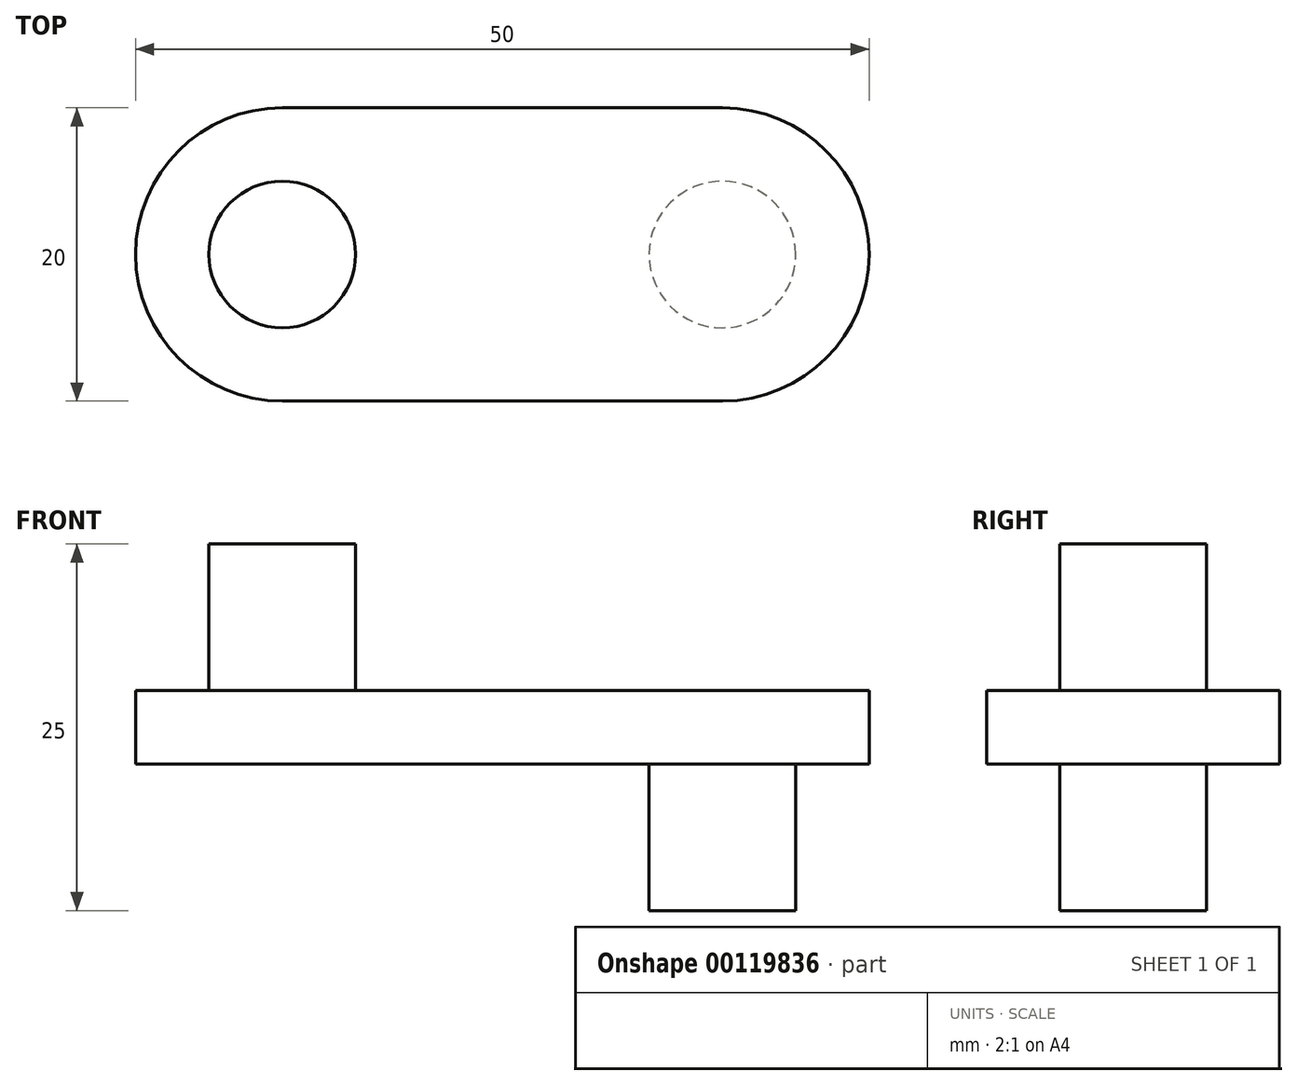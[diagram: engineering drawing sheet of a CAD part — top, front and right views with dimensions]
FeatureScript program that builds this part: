
annotation { "Feature Type Name" : "Feature", "Feature Type Description" : "" }
export const myFeature = defineFeature(function(context is Context, id is Id, definition is map)
    precondition{}
    {
        {
            var Q0;
            Q0=qCreatedBy(makeId("Top.planeOp"),FACE);
            var sketch = newSketch(context, id + "F0", { "sketchPlane" : qUnion([Q0])});
            skLineSegment(sketch, "E0.bottom", {"start": v(0, 0) * mm, "end": v(30, 0) * mm});
            skLineSegment(sketch, "E0.top", {"start": v(0, 20) * mm, "end": v(30, 20) * mm});
            skLineSegment(sketch, "E0.left", {"start": v(0, 0) * mm, "end": v(0, 20) * mm});
            skLineSegment(sketch, "E0.right", {"start": v(30, 0) * mm, "end": v(30, 20) * mm});
            skArc(sketch, "E1", {"start": v(0, 20) * mm, "mid": v(-10, 10) * mm, "end": v(0, 0) * mm});
            skArc(sketch, "E2", {"start": v(30, 0) * mm, "mid": v(40, 10) * mm, "end": v(30, 20) * mm});
            skCircle(sketch, "E3", {"center": v(0, 10) * mm, "radius": 5 * mm});
            skCircle(sketch, "E4", {"center": v(30, 10) * mm, "radius": 5 * mm});
            skSolve(sketch);
        }
        {
            var Q0;
            {var subQ5=sQuery(id+"F0.wireOp",EDGE,"E0.bottom");Q0=makeQuery(id+"F0.imprint","IMPRINT",FACE,{"disambiguationData":[TD([[makeQuery(id+"F0.imprint","IMPRINT",EDGE,{"derivedFrom":subQ5}),1.0]])]});}
            var Q1;
            {var subQ0=sQuery(id+"F0.wireOp",EDGE,"E1");Q1=makeQuery(id+"F0.imprint","IMPRINT",FACE,{"disambiguationData":[TD([[makeQuery(id+"F0.imprint","IMPRINT",EDGE,{"derivedFrom":subQ0}),1.0]])]});}
            var Q2;
            {var subQ0=sQuery(id+"F0.wireOp",EDGE,"E2");Q2=makeQuery(id+"F0.imprint","IMPRINT",FACE,{"disambiguationData":[TD([[makeQuery(id+"F0.imprint","IMPRINT",EDGE,{"derivedFrom":subQ0}),1.0]])]});}
            extrude(context, id + "F1", {"entities" : qUnion([Q0, Q1, Q2]), "depth" : 5 * mm});
        }
        {
            var Q0;
            {var subQ0=sQuery(id+"F0.wireOp",EDGE,"E3");var subQ1=sQuery(id+"F0.wireOp",EDGE,"E0.left");var subQ2=makeQuery(id+"F0.imprint","INTERSECT",VERTEX,{"disambiguationData":[OD(0.0)],"derivedFrom":[subQ1,subQ0]});Q0=makeQuery(id+"F0.imprint","IMPRINT",FACE,{"disambiguationData":[TD([[makeQuery(id+"F0.imprint","IMPRINT",EDGE,{"disambiguationData":[TD([[subQ2,-1.0]])],"derivedFrom":subQ1}),1.0]])]});}
            var Q1;
            {var subQ0=sQuery(id+"F0.wireOp",EDGE,"E3");var subQ1=sQuery(id+"F0.wireOp",EDGE,"E0.left");var subQ2=makeQuery(id+"F0.imprint","INTERSECT",VERTEX,{"disambiguationData":[OD(0.0)],"derivedFrom":[subQ1,subQ0]});Q1=makeQuery(id+"F0.imprint","IMPRINT",FACE,{"disambiguationData":[TD([[makeQuery(id+"F0.imprint","IMPRINT",EDGE,{"disambiguationData":[TD([[subQ2,-1.0]])],"derivedFrom":subQ1}),-1.0]])]});}
            extrude(context, id + "F2", {"entities" : qUnion([Q0, Q1]), "operationType" : NewBodyOperationType.ADD, "depth" : 15 * mm});
        }
        {
            var Q0;
            {var subQ0=sQuery(id+"F0.wireOp",EDGE,"E4");var subQ1=sQuery(id+"F0.wireOp",EDGE,"E0.right");var subQ2=makeQuery(id+"F0.imprint","INTERSECT",VERTEX,{"disambiguationData":[OD(0.0)],"derivedFrom":[subQ1,subQ0]});Q0=makeQuery(id+"F0.imprint","IMPRINT",FACE,{"disambiguationData":[TD([[makeQuery(id+"F0.imprint","IMPRINT",EDGE,{"disambiguationData":[TD([[subQ2,-1.0]])],"derivedFrom":subQ1}),1.0]])]});}
            var Q1;
            {var subQ0=sQuery(id+"F0.wireOp",EDGE,"E4");var subQ1=sQuery(id+"F0.wireOp",EDGE,"E0.right");var subQ2=makeQuery(id+"F0.imprint","INTERSECT",VERTEX,{"disambiguationData":[OD(0.0)],"derivedFrom":[subQ1,subQ0]});Q1=makeQuery(id+"F0.imprint","IMPRINT",FACE,{"disambiguationData":[TD([[makeQuery(id+"F0.imprint","IMPRINT",EDGE,{"disambiguationData":[TD([[subQ2,-1.0]])],"derivedFrom":subQ1}),-1.0]])]});}
            extrude(context, id + "F3", {"entities" : qUnion([Q0, Q1]), "operationType" : NewBodyOperationType.ADD, "oppositeDirection" : true, "depth" : 10 * mm, "hasSecondDirection" : true, "secondDirectionOppositeDirection" : false, "secondDirectionDepth" : 5 * mm});
        }
    });
